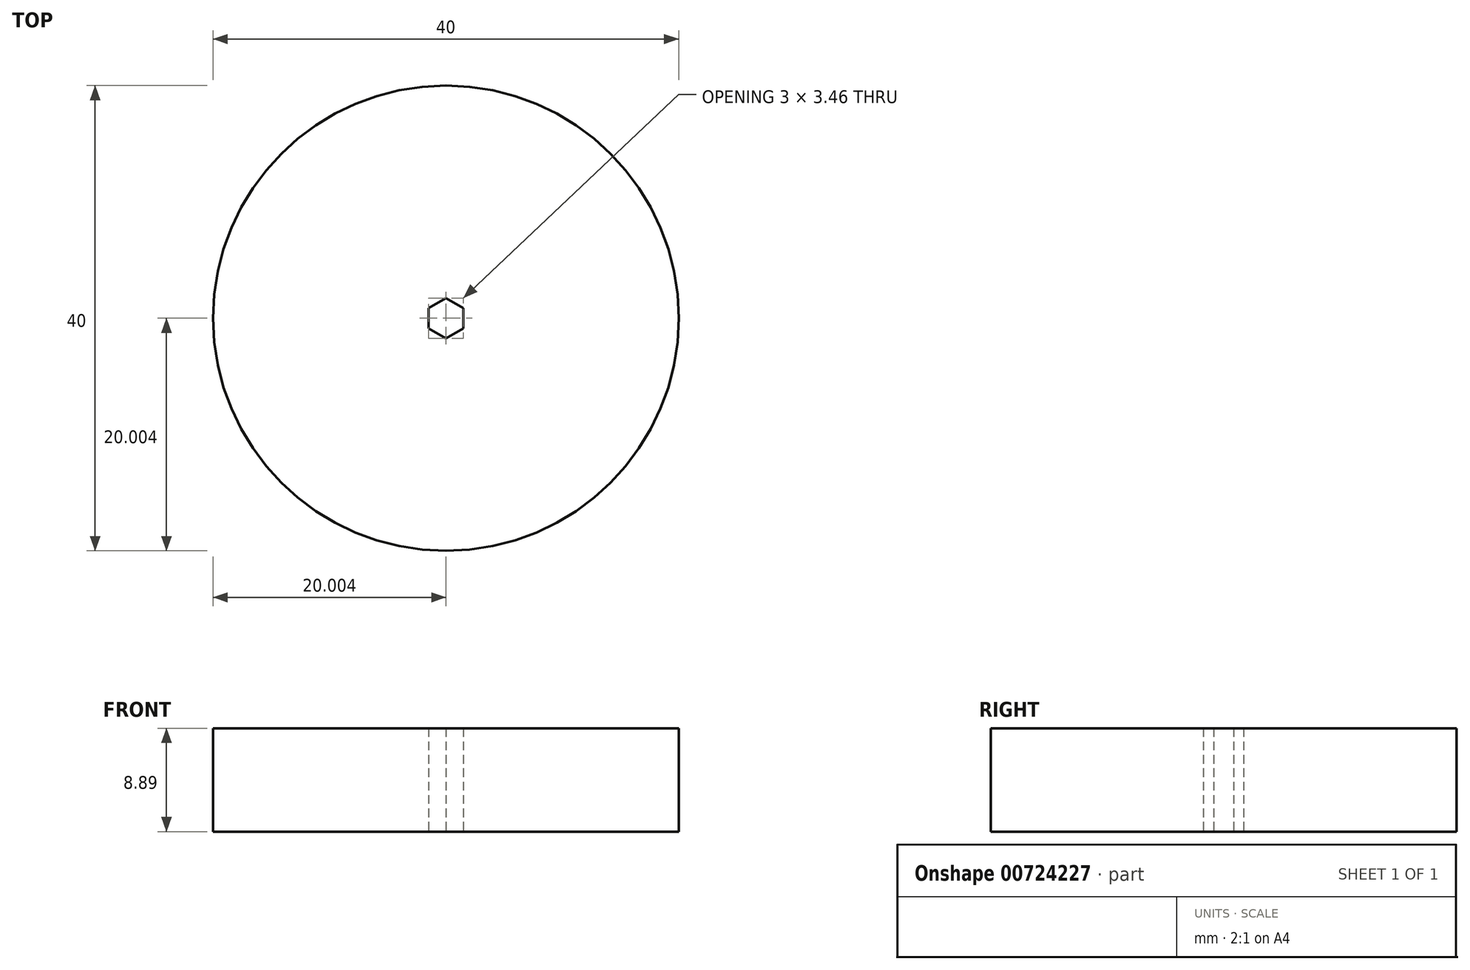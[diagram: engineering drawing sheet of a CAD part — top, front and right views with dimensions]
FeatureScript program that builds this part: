
annotation { "Feature Type Name" : "Feature", "Feature Type Description" : "" }
export const myFeature = defineFeature(function(context is Context, id is Id, definition is map)
    precondition{}
    {
        {
            var Q0;
            Q0=qCreatedBy(makeId("Top.planeOp"),FACE);
            var sketch = newSketch(context, id + "F0", { "sketchPlane" : qUnion([Q0])});
            skCircle(sketch, "E0", {"center": v(-29.04, 28.76) * mm, "radius": 20 * mm});
            skCircle(sketch, "E1.cCircle", {"center": v(-29.04, 28.76) * mm, "radius": 1.5 * mm, "construction": true});
            skLineSegment(sketch, "E1.0", {"start": v(-27.54, 29.63) * mm, "end": v(-27.54, 27.9) * mm});
            skLineSegment(sketch, "E1.1", {"start": v(-27.54, 27.9) * mm, "end": v(-29.04, 27.03) * mm});
            skLineSegment(sketch, "E1.2", {"start": v(-29.04, 27.03) * mm, "end": v(-30.54, 27.9) * mm});
            skLineSegment(sketch, "E1.3", {"start": v(-30.54, 27.9) * mm, "end": v(-30.54, 29.63) * mm});
            skLineSegment(sketch, "E1.4", {"start": v(-30.54, 29.63) * mm, "end": v(-29.04, 30.5) * mm});
            skLineSegment(sketch, "E1.5", {"start": v(-29.04, 30.5) * mm, "end": v(-27.54, 29.63) * mm});
            skSolve(sketch);
        }
        {
            var Q0;
            Q0 = qSketchRegion(id + "F0", true);
            extrude(context, id + "F1", {"entities" : qUnion([Q0]), "depth" : 8.9 * mm, "offsetDistance" : 25.4 * mm});
        }
        {
            var Q0;
            Q0=makeQuery(id+"F0.imprint","IMPRINT",FACE,{"disambiguationData":[TD([[makeQuery(id+"F0.imprint","IMPRINT",EDGE,{"derivedFrom":sQuery(id+"F0.wireOp",EDGE,"E1.0")}),-1.0]])]});
            extrude(context, id + "F2", {"entities" : qUnion([Q0]), "operationType" : NewBodyOperationType.REMOVE, "depth" : 8.9 * mm, "offsetDistance" : 25.4 * mm});
        }
    });
